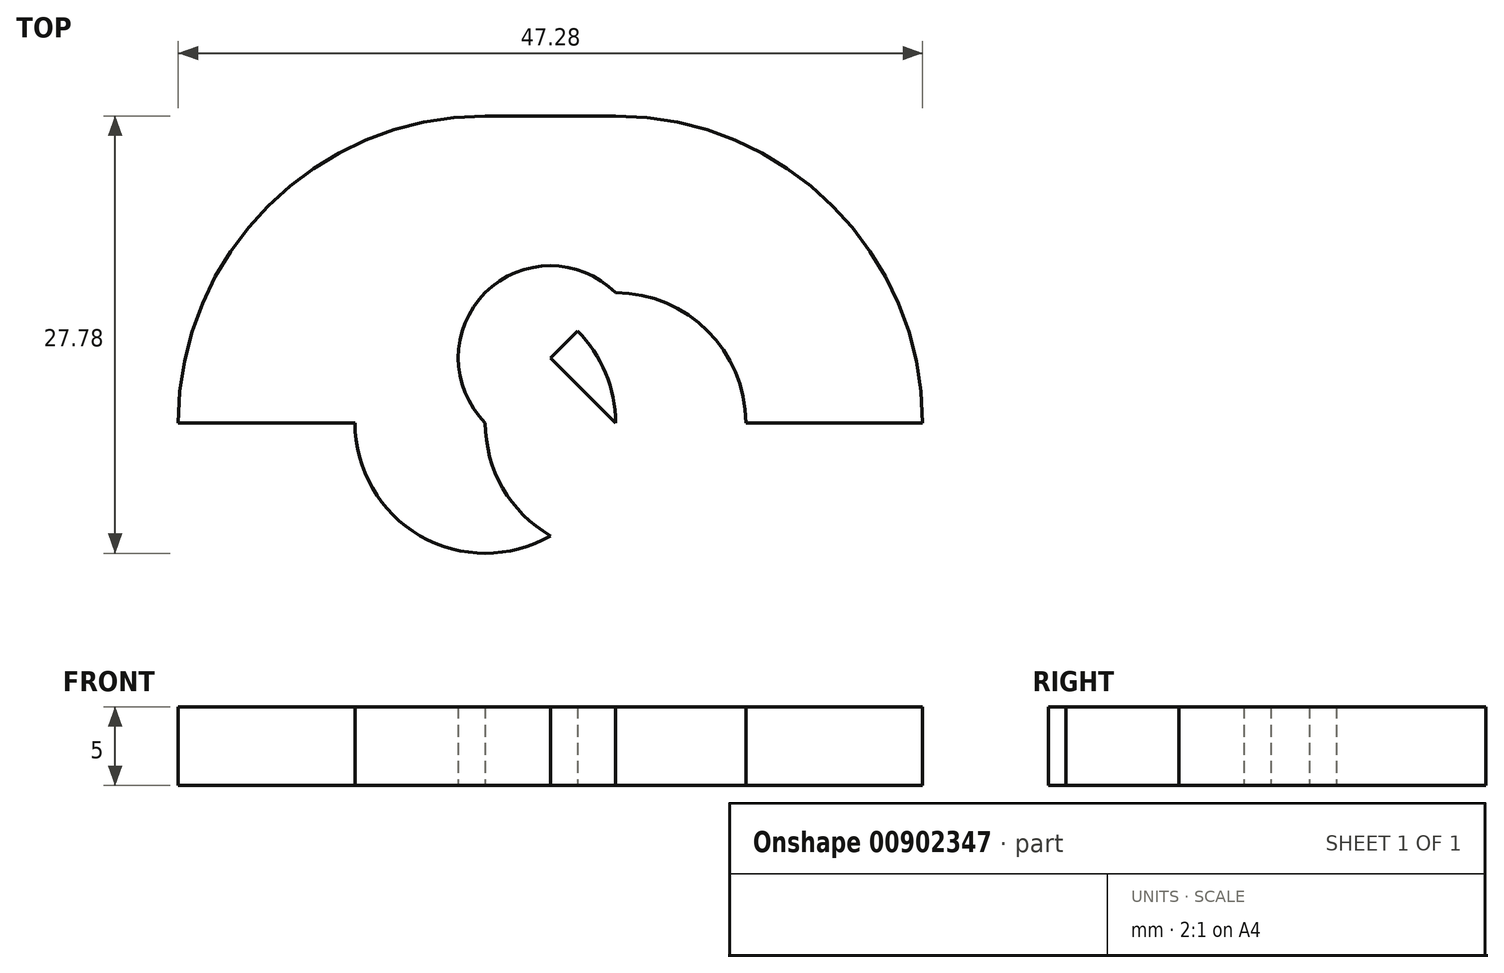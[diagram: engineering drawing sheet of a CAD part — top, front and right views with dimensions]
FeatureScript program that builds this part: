
annotation { "Feature Type Name" : "Feature", "Feature Type Description" : "" }
export const myFeature = defineFeature(function(context is Context, id is Id, definition is map)
    precondition{}
    {
        {
            var Q0;
            Q0=qCreatedBy(makeId("Top.planeOp"),FACE);
            var sketch = newSketch(context, id + "F0", { "sketchPlane" : qUnion([Q0])});
            skLineSegment(sketch, "E0.bottom", {"start": v(4.14, -9.75) * mm, "end": v(-4.14, -9.75) * mm});
            skLineSegment(sketch, "E0.top", {"start": v(4.14, 9.75) * mm, "end": v(-4.14, 9.75) * mm});
            skLineSegment(sketch, "E0.left", {"start": v(4.14, -9.75) * mm, "end": v(4.14, 9.75) * mm});
            skLineSegment(sketch, "E0.right", {"start": v(-4.14, -9.75) * mm, "end": v(-4.14, 9.75) * mm});
            skPoint(sketch, "E0.middle", {"position": v(0, 0) * mm});
            skCircle(sketch, "E1", {"center": v(4.14, -9.75) * mm, "radius": 19.5 * mm});
            skCircle(sketch, "E2", {"center": v(-4.14, -9.75) * mm, "radius": 19.5 * mm});
            skLineSegment(sketch, "E3", {"start": v(9.84, -9.75) * mm, "end": v(23.64, -9.75) * mm});
            skLineSegment(sketch, "E4", {"start": v(23.64, -9.75) * mm, "end": v(-23.64, -9.75) * mm});
            skLineSegment(sketch, "E5", {"start": v(-4.14, -9.75) * mm, "end": v(-4.14, -35.21) * mm});
            skLineSegment(sketch, "E6", {"start": v(4.14, -9.75) * mm, "end": v(4.14, -35.21) * mm});
            skLineSegment(sketch, "E7", {"start": v(23.64, -9.75) * mm, "end": v(67.44, -9.75) * mm});
            skLineSegment(sketch, "E8", {"start": v(67.44, -9.75) * mm, "end": v(-46.07, -9.75) * mm});
            skCircle(sketch, "E9", {"center": v(4.14, -9.75) * mm, "radius": 8.28 * mm});
            skCircle(sketch, "E10", {"center": v(-4.14, -9.75) * mm, "radius": 8.28 * mm});
            skLineSegment(sketch, "E11", {"start": v(-4.14, -9.75) * mm, "end": v(4.14, -1.47) * mm});
            skLineSegment(sketch, "E12", {"start": v(4.14, -9.75) * mm, "end": v(-4.14, -1.47) * mm});
            skCircle(sketch, "E13", {"center": v(0, -5.61) * mm, "radius": 5.85 * mm});
            skSolve(sketch);
        }
        {
            var Q0;
            {var subQ1=sQuery(id+"F0.wireOp",EDGE,"E0.right");var subQ3=sQuery(id+"F0.wireOp",EDGE,"E1");var subQ4=makeQuery(id+"F0.imprint","INTERSECT",VERTEX,{"derivedFrom":[subQ1,subQ3]});Q0=makeQuery(id+"F0.imprint","IMPRINT",FACE,{"disambiguationData":[TD([[makeQuery(id+"F0.imprint","IMPRINT",EDGE,{"disambiguationData":[TD([[subQ4,-1.0]])],"derivedFrom":subQ3}),-1.0]])]});}
            var Q1;
            {var subQ1=sQuery(id+"F0.wireOp",EDGE,"E0.right");var subQ3=sQuery(id+"F0.wireOp",EDGE,"E1");var subQ4=makeQuery(id+"F0.imprint","INTERSECT",VERTEX,{"derivedFrom":[subQ1,subQ3]});Q1=makeQuery(id+"F0.imprint","IMPRINT",FACE,{"disambiguationData":[TD([[makeQuery(id+"F0.imprint","IMPRINT",EDGE,{"disambiguationData":[TD([[subQ4,-1.0]])],"derivedFrom":subQ3}),1.0]])]});}
            var Q2;
            {var subQ1=sQuery(id+"F0.wireOp",EDGE,"E8");var subQ4=sQuery(id+"F0.wireOp",EDGE,"E10");var subQ5=makeQuery(id+"F0.imprint","INTERSECT",VERTEX,{"derivedFrom":[subQ1,subQ4]});Q2=makeQuery(id+"F0.imprint","IMPRINT",FACE,{"disambiguationData":[TD([[makeQuery(id+"F0.imprint","IMPRINT",EDGE,{"disambiguationData":[TD([[subQ5,1.0]])],"derivedFrom":subQ4}),1.0]])]});}
            var Q3;
            {var subQ3=sQuery(id+"F0.wireOp",EDGE,"E1");var subQ6=sQuery(id+"F0.wireOp",EDGE,"E0.right");var subQ8=makeQuery(id+"F0.imprint","INTERSECT",VERTEX,{"derivedFrom":[subQ6,subQ3]});Q3=makeQuery(id+"F0.imprint","IMPRINT",FACE,{"disambiguationData":[TD([[makeQuery(id+"F0.imprint","IMPRINT",EDGE,{"disambiguationData":[TD([[subQ8,1.0]])],"derivedFrom":subQ3}),1.0]])]});}
            var Q4;
            {var subQ1=sQuery(id+"F0.wireOp",EDGE,"E0.left");var subQ3=sQuery(id+"F0.wireOp",EDGE,"E2");var subQ4=makeQuery(id+"F0.imprint","INTERSECT",VERTEX,{"derivedFrom":[subQ1,subQ3]});Q4=makeQuery(id+"F0.imprint","IMPRINT",FACE,{"disambiguationData":[TD([[makeQuery(id+"F0.imprint","IMPRINT",EDGE,{"disambiguationData":[TD([[subQ4,-1.0]])],"derivedFrom":subQ3}),-1.0]])]});}
            var Q5;
            {var subQ0=sQuery(id+"F0.wireOp",EDGE,"E0.top");Q5=makeQuery(id+"F0.imprint","IMPRINT",FACE,{"disambiguationData":[TD([[makeQuery(id+"F0.imprint","IMPRINT",EDGE,{"derivedFrom":subQ0}),1.0]])]});}
            var Q6;
            {var subQ1=sQuery(id+"F0.wireOp",EDGE,"E0.right");var subQ3=sQuery(id+"F0.wireOp",EDGE,"E1");var subQ4=makeQuery(id+"F0.imprint","INTERSECT",VERTEX,{"derivedFrom":[subQ1,subQ3]});Q6=makeQuery(id+"F0.imprint","IMPRINT",FACE,{"disambiguationData":[TD([[makeQuery(id+"F0.imprint","IMPRINT",EDGE,{"disambiguationData":[TD([[subQ4,1.0]])],"derivedFrom":subQ3}),-1.0]])]});}
            var Q7;
            {var subQ1=sQuery(id+"F0.wireOp",EDGE,"E0.left");var subQ3=sQuery(id+"F0.wireOp",EDGE,"E2");var subQ4=makeQuery(id+"F0.imprint","INTERSECT",VERTEX,{"derivedFrom":[subQ1,subQ3]});Q7=makeQuery(id+"F0.imprint","IMPRINT",FACE,{"disambiguationData":[TD([[makeQuery(id+"F0.imprint","IMPRINT",EDGE,{"disambiguationData":[TD([[subQ4,1.0]])],"derivedFrom":subQ3}),1.0]])]});}
            var Q8;
            {var subQ0=sQuery(id+"F0.wireOp",EDGE,"E8");var subQ1=makeQuery(id+"F0.imprint","IMPRINT",VERTEX,{"derivedFrom":subQ0});Q8=makeQuery(id+"F0.imprint","IMPRINT",FACE,{"disambiguationData":[TD([[makeQuery(id+"F0.imprint","IMPRINT",EDGE,{"disambiguationData":[TD([[subQ1,1.0]])],"derivedFrom":subQ0}),-1.0]])]});}
            var Q9;
            {var subQ1=sQuery(id+"F0.wireOp",EDGE,"E0.left");var subQ3=sQuery(id+"F0.wireOp",EDGE,"E2");var subQ4=makeQuery(id+"F0.imprint","INTERSECT",VERTEX,{"derivedFrom":[subQ1,subQ3]});Q9=makeQuery(id+"F0.imprint","IMPRINT",FACE,{"disambiguationData":[TD([[makeQuery(id+"F0.imprint","IMPRINT",EDGE,{"disambiguationData":[TD([[subQ4,1.0]])],"derivedFrom":subQ3}),-1.0]])]});}
            extrude(context, id + "F1", {"entities" : qUnion([Q0, Q1, Q2, Q3, Q4, Q5, Q6, Q7, Q8, Q9]), "depth" : 5 * mm, "offsetDistance" : 25 * mm});
        }
    });
